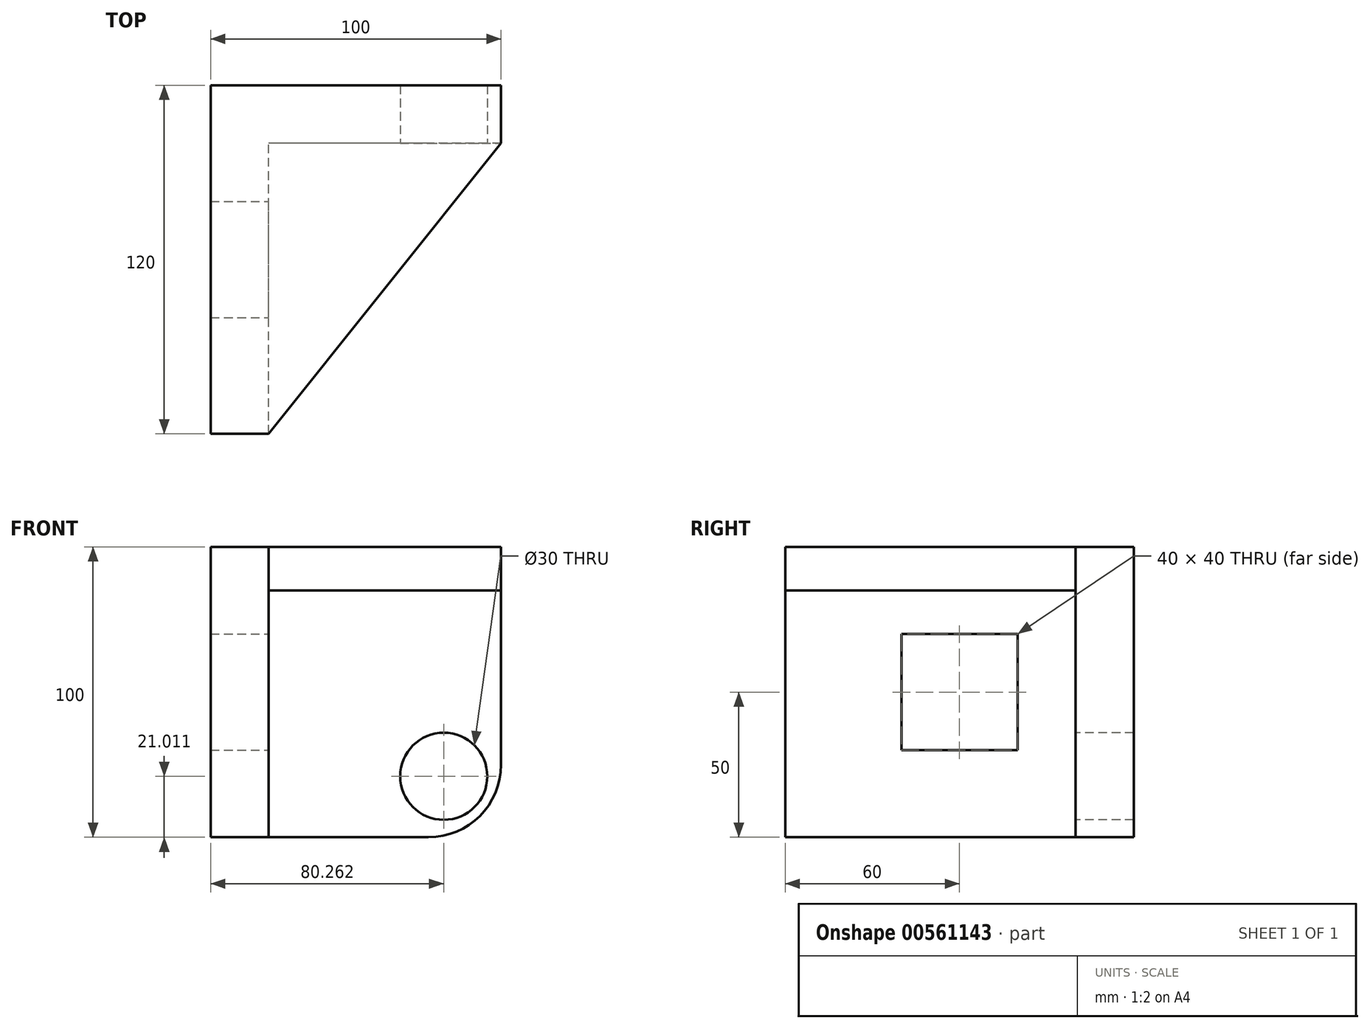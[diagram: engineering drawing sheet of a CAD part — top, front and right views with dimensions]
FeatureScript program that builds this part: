
annotation { "Feature Type Name" : "Feature", "Feature Type Description" : "" }
export const myFeature = defineFeature(function(context is Context, id is Id, definition is map)
    precondition{}
    {
        {
            var Q0;
            Q0=qCreatedBy(makeId("Front.planeOp"),FACE);
            var sketch = newSketch(context, id + "F0", { "sketchPlane" : qUnion([Q0])});
            skLineSegment(sketch, "E0.bottom", {"start": v(50, 50) * mm, "end": v(-50, 50) * mm});
            skLineSegment(sketch, "E0.top", {"start": v(50, -50) * mm, "end": v(-50, -50) * mm});
            skLineSegment(sketch, "E0.left", {"start": v(50, 50) * mm, "end": v(50, -50) * mm});
            skLineSegment(sketch, "E0.right", {"start": v(-50, 50) * mm, "end": v(-50, -50) * mm});
            skPoint(sketch, "E0.middle", {"position": v(0, 0) * mm});
            skSolve(sketch);
        }
        {
            var Q0;
            Q0 = qSketchRegion(id + "F0", true);
            extrude(context, id + "F1", {"entities" : qUnion([Q0]), "depth" : 20 * mm, "offsetDistance" : 25 * mm});
        }
        {
            var Q0;
            Q0=makeQuery(id+"F1.opExtrude","CAP_FACE",FACE,{"disambiguationData":[OSD([sQuery(id+"F0.wireOp",EDGE,"E0.bottom"),sQuery(id+"F0.wireOp",EDGE,"E0.top"),sQuery(id+"F0.wireOp",EDGE,"E0.left"),sQuery(id+"F0.wireOp",EDGE,"E0.right")])],"isStart":false});
            var sketch = newSketch(context, id + "F2", { "sketchPlane" : qUnion([Q0])});
            skCircle(sketch, "E1", {"center": v(30.26, -28.99) * mm, "radius": 15 * mm});
            skPoint(sketch, "E1.first.point", {"position": v(21.85, -16.57) * mm});
            skPoint(sketch, "E1.second.point", {"position": v(39.88, -40.5) * mm});
            skPoint(sketch, "E1.third.point", {"position": v(43, -21.08) * mm});
            skSolve(sketch);
        }
        {
            var Q0;
            Q0=makeQuery(id+"F2.imprint","IMPRINT",FACE,{"disambiguationData":[TD([[makeQuery(id+"F2.imprint","IMPRINT",EDGE,{"derivedFrom":sQuery(id+"F2.wireOp",EDGE,"E1")}),1.0]])]});
            extrude(context, id + "F3", {"entities" : qUnion([Q0]), "operationType" : NewBodyOperationType.REMOVE, "oppositeDirection" : true, "depth" : 20 * mm, "offsetDistance" : 25 * mm});
        }
        {
            var Q0;
            Q0=makeQuery(id+"F1.opExtrude","CAP_FACE",FACE,{"disambiguationData":[OSD([sQuery(id+"F0.wireOp",EDGE,"E0.bottom"),sQuery(id+"F0.wireOp",EDGE,"E0.top"),sQuery(id+"F0.wireOp",EDGE,"E0.left"),sQuery(id+"F0.wireOp",EDGE,"E0.right")])],"isStart":false});
            var sketch = newSketch(context, id + "F4", { "sketchPlane" : qUnion([Q0])});
            skLineSegment(sketch, "E2", {"start": v(-50, 50) * mm, "end": v(-30, 50) * mm});
            skLineSegment(sketch, "E3", {"start": v(-30, 50) * mm, "end": v(-30, -50) * mm});
            skLineSegment(sketch, "E4", {"start": v(-50, 50) * mm, "end": v(-50, -50) * mm});
            skSolve(sketch);
        }
        {
            var Q0;
            Q0=makeQuery(id+"F4.imprint","IMPRINT",FACE,{"disambiguationData":[TD([[makeQuery(id+"F4.imprint","IMPRINT",EDGE,{"derivedFrom":sQuery(id+"F4.wireOp",EDGE,"E2")}),1.0]])]});
            extrude(context, id + "F5", {"entities" : qUnion([Q0]), "operationType" : NewBodyOperationType.ADD, "depth" : 100 * mm, "offsetDistance" : 25 * mm});
        }
        {
            var Q0;
            Q0=makeQuery(id+"F1.opExtrude","SWEPT_EDGE",EDGE,{"disambiguationData":[OSD([sQuery(id+"F0.wireOp",EDGE,"E0.top"),sQuery(id+"F0.wireOp",EDGE,"E0.left")])]});
            fillet(context, id + "F6", {"entities" : qUnion([Q0]), "radius" : 25 * mm, "tangentPropagation" : true, "allowEdgeOverflow" : false});
        }
        {
            var Q0;
            Q0=makeQuery(id+"F5.opExtrude","SWEPT_FACE",FACE,{"disambiguationData":[OSD([sQuery(id+"F4.wireOp",EDGE,"E3")])]});
            var sketch = newSketch(context, id + "F7", { "sketchPlane" : qUnion([Q0])});
            skLineSegment(sketch, "E5", {"start": v(0, 50) * mm, "end": v(-120, 50) * mm});
            skLineSegment(sketch, "E6", {"start": v(-120, 50) * mm, "end": v(-120, -50) * mm});
            skLineSegment(sketch, "E7", {"start": v(0, -50) * mm, "end": v(0, 50) * mm});
            skLineSegment(sketch, "E8", {"start": v(0, 50) * mm, "end": v(-60, 50) * mm});
            skPoint(sketch, "E8.endSnap0", {"position": v(-60, 50) * mm});
            skLineSegment(sketch, "E9.bottom", {"start": v(-80, -20) * mm, "end": v(-40, -20) * mm});
            skLineSegment(sketch, "E9.top", {"start": v(-80, 20) * mm, "end": v(-40, 20) * mm});
            skLineSegment(sketch, "E9.left", {"start": v(-80, -20) * mm, "end": v(-80, 20) * mm});
            skLineSegment(sketch, "E9.right", {"start": v(-40, -20) * mm, "end": v(-40, 20) * mm});
            skPoint(sketch, "E9.middle", {"position": v(-60, 0) * mm});
            skSolve(sketch);
        }
        {
            var Q0;
            Q0=makeQuery(id+"F7.imprint","IMPRINT",FACE,{"disambiguationData":[TD([[makeQuery(id+"F7.imprint","IMPRINT",EDGE,{"derivedFrom":sQuery(id+"F7.wireOp",EDGE,"E9.bottom")}),1.0]])]});
            extrude(context, id + "F8", {"entities" : qUnion([Q0]), "operationType" : NewBodyOperationType.REMOVE, "oppositeDirection" : true, "depth" : 20 * mm, "offsetDistance" : 25 * mm});
        }
        {
            var Q0;
            Q0=makeQuery(id+"F5.boolean.opBoolean","MERGE",FACE,{"derivedFrom":[makeQuery(id+"F1.opExtrude","SWEPT_FACE",FACE,{"disambiguationData":[OSD([sQuery(id+"F0.wireOp",EDGE,"E0.bottom")])]}),makeQuery(id+"F5.opExtrude","SWEPT_FACE",FACE,{"disambiguationData":[OSD([sQuery(id+"F4.wireOp",EDGE,"E2")])]})]});
            var sketch = newSketch(context, id + "F9", { "sketchPlane" : qUnion([Q0])});
            skLineSegment(sketch, "E10", {"start": v(-30, -120) * mm, "end": v(50, -20) * mm});
            skSolve(sketch);
        }
        {
            var Q0;
            Q0=makeQuery(id+"F9.imprint","IMPRINT",FACE,{"disambiguationData":[TD([[makeQuery(id+"F9.imprint","IMPRINT",EDGE,{"derivedFrom":sQuery(id+"F9.wireOp",EDGE,"E10")}),1.0]])]});
            extrude(context, id + "F10", {"entities" : qUnion([Q0]), "operationType" : NewBodyOperationType.ADD, "oppositeDirection" : true, "depth" : 15 * mm, "offsetDistance" : 25 * mm});
        }
    });
